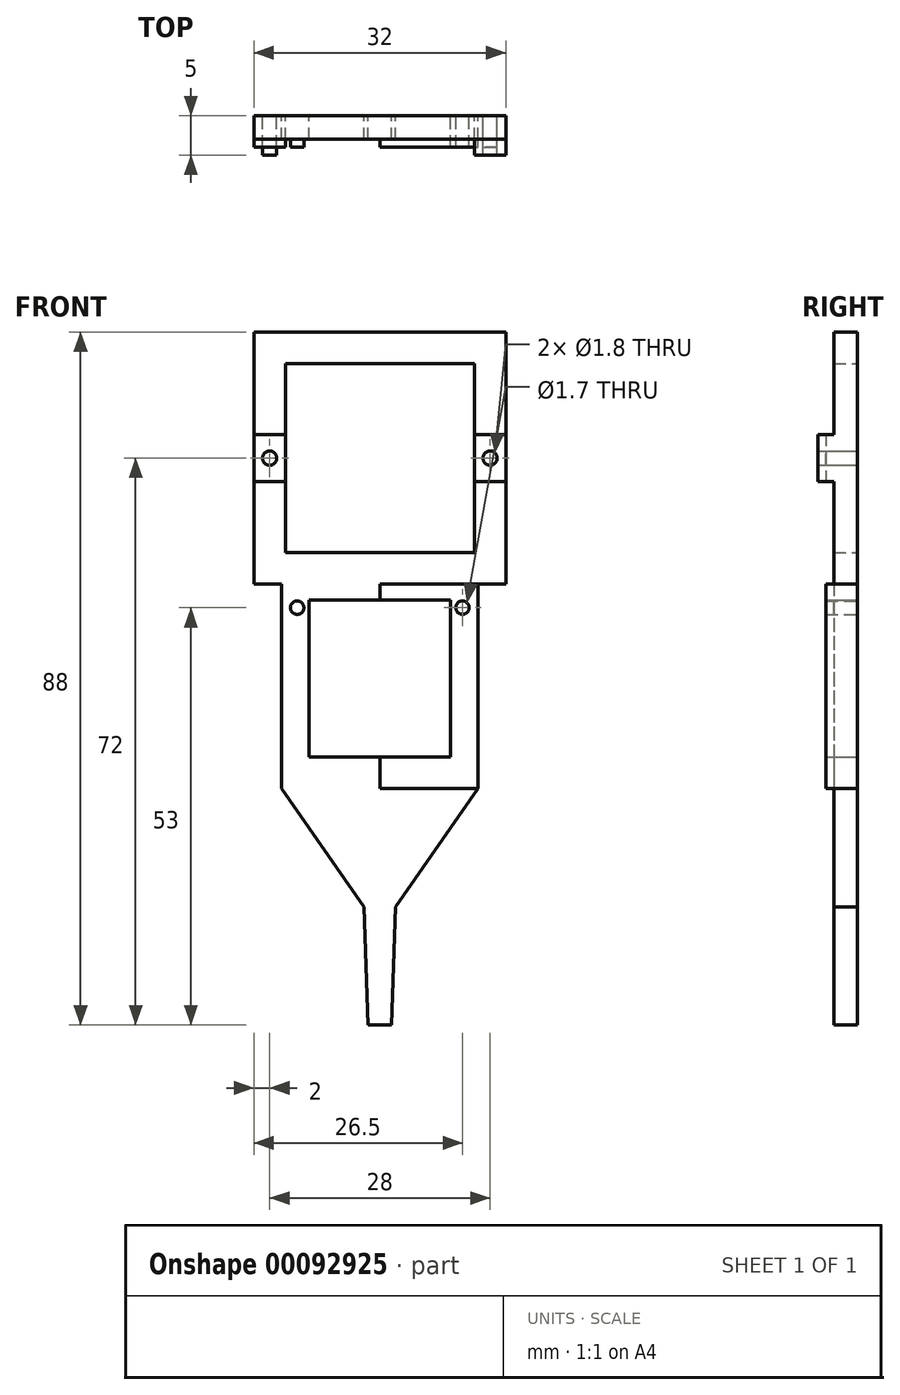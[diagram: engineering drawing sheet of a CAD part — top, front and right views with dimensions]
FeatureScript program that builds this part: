
annotation { "Feature Type Name" : "Feature", "Feature Type Description" : "" }
export const myFeature = defineFeature(function(context is Context, id is Id, definition is map)
    precondition{}
    {
        {
            var Q0;
            Q0=qCreatedBy(makeId("Front.planeOp"),FACE);
            var sketch = newSketch(context, id + "F0", { "sketchPlane" : qUnion([Q0])});
            skLineSegment(sketch, "E0.bottom", {"start": v(-12.5, -4) * mm, "end": v(12.5, -4) * mm});
            skLineSegment(sketch, "E0.top", {"start": v(-12.5, -30) * mm, "end": v(12.5, -30) * mm});
            skLineSegment(sketch, "E0.left", {"start": v(-12.5, -4) * mm, "end": v(-12.5, -30) * mm});
            skLineSegment(sketch, "E0.right", {"start": v(12.5, -4) * mm, "end": v(12.5, -30) * mm});
            skCircle(sketch, "E1", {"center": v(-10.5, -7) * mm, "radius": 0.85 * mm});
            skLineSegment(sketch, "E2", {"start": v(0, 31.04) * mm, "end": v(0, -38.81) * mm});
            skCircle(sketch, "E3.MirrorC", {"center": v(10.5, -7) * mm, "radius": 0.85 * mm});
            skLineSegment(sketch, "E4.bottom", {"start": v(-9, -6) * mm, "end": v(9, -6) * mm});
            skLineSegment(sketch, "E4.top", {"start": v(-9, -26) * mm, "end": v(9, -26) * mm});
            skLineSegment(sketch, "E4.left", {"start": v(-9, -6) * mm, "end": v(-9, -26) * mm});
            skLineSegment(sketch, "E4.right", {"start": v(9, -6) * mm, "end": v(9, -26) * mm});
            skLineSegment(sketch, "E5.MirrorCS", {"start": v(9, -6) * mm, "end": v(-9, -6) * mm});
            skLineSegment(sketch, "E6.MirrorCS", {"start": v(9, -26) * mm, "end": v(-9, -26) * mm});
            skLineSegment(sketch, "E7.bottom", {"start": v(-16, 28) * mm, "end": v(16, 28) * mm});
            skLineSegment(sketch, "E7.top", {"start": v(-16, -4) * mm, "end": v(16, -4) * mm});
            skLineSegment(sketch, "E7.left", {"start": v(-16, 28) * mm, "end": v(-16, -4) * mm});
            skLineSegment(sketch, "E8.bottom", {"start": v(-12, 24) * mm, "end": v(12, 24) * mm});
            skLineSegment(sketch, "E8.top", {"start": v(-12, 0) * mm, "end": v(12, 0) * mm});
            skLineSegment(sketch, "E8.left", {"start": v(-12, 24) * mm, "end": v(-12, 0) * mm});
            skLineSegment(sketch, "E8.right", {"start": v(12, 24) * mm, "end": v(12, 0) * mm});
            skCircle(sketch, "E9", {"center": v(-14, 12) * mm, "radius": 0.9 * mm});
            skLineSegment(sketch, "E10.MirrorCS", {"start": v(0, -39.04) * mm, "end": v(0, 30.81) * mm});
            skCircle(sketch, "E11.MirrorC", {"center": v(14, 12) * mm, "radius": 0.9 * mm});
            skLineSegment(sketch, "E12.bottom", {"start": v(-2, -45) * mm, "end": v(2, -45) * mm});
            skLineSegment(sketch, "E13", {"start": v(-12.5, -30) * mm, "end": v(-2, -45) * mm});
            skLineSegment(sketch, "E14", {"start": v(12.5, -30) * mm, "end": v(2, -45) * mm});
            skLineSegment(sketch, "E15.top", {"start": v(12, 9) * mm, "end": v(16, 9) * mm});
            skLineSegment(sketch, "E15.left", {"start": v(12, 15) * mm, "end": v(12, 9) * mm});
            skLineSegment(sketch, "E15.right", {"start": v(16, 15) * mm, "end": v(16, 9) * mm});
            skLineSegment(sketch, "E16.bottom", {"start": v(-16, 15) * mm, "end": v(-12, 15) * mm});
            skLineSegment(sketch, "E16.top", {"start": v(-16, 9) * mm, "end": v(-12, 9) * mm});
            skLineSegment(sketch, "E16.left", {"start": v(-16, 15) * mm, "end": v(-16, 9) * mm});
            skLineSegment(sketch, "E16.right", {"start": v(-12, 15) * mm, "end": v(-12, 9) * mm});
            skLineSegment(sketch, "E17.bottom", {"start": v(12, 15) * mm, "end": v(16, 15) * mm});
            skLineSegment(sketch, "E18", {"start": v(-2, -45) * mm, "end": v(-1.5, -60) * mm});
            skLineSegment(sketch, "E19", {"start": v(-1.5, -60) * mm, "end": v(1.5, -60) * mm});
            skLineSegment(sketch, "E20", {"start": v(1.5, -60) * mm, "end": v(2, -45) * mm});
            skLineSegment(sketch, "E21", {"start": v(16, -4) * mm, "end": v(16, 28) * mm});
            skSolve(sketch);
        }
        {
            var Q0;
            Q0=makeQuery(id+"F0.imprint","IMPRINT",FACE,{"disambiguationData":[TD([[makeQuery(id+"F0.imprint","IMPRINT",EDGE,{"derivedFrom":sQuery(id+"F0.wireOp",EDGE,"E9")}),1.0]])]});
            var Q1;
            Q1=makeQuery(id+"F0.imprint","IMPRINT",FACE,{"disambiguationData":[TD([[makeQuery(id+"F0.imprint","IMPRINT",EDGE,{"derivedFrom":sQuery(id+"F0.wireOp",EDGE,"E11.MirrorC")}),-1.0]])]});
            extrude(context, id + "F1", {"entities" : qUnion([Q0, Q1]), "depth" : 5 * mm});
        }
        {
            var Q0;
            Q0=makeQuery(id+"F0.imprint","IMPRINT",FACE,{"disambiguationData":[TD([[makeQuery(id+"F0.imprint","IMPRINT",EDGE,{"derivedFrom":sQuery(id+"F0.wireOp",EDGE,"E1")}),1.0]])]});
            var Q1;
            Q1=makeQuery(id+"F0.imprint","IMPRINT",FACE,{"disambiguationData":[TD([[makeQuery(id+"F0.imprint","IMPRINT",EDGE,{"derivedFrom":sQuery(id+"F0.wireOp",EDGE,"42e0c05e-9e20-4baa-a6e4-a09fdd3b6eb8")}),1.0]])]});
            var Q2;
            Q2=makeQuery(id+"F0.imprint","IMPRINT",FACE,{"disambiguationData":[TD([[makeQuery(id+"F0.imprint","IMPRINT",EDGE,{"derivedFrom":sQuery(id+"F0.wireOp",EDGE,"E3.MirrorC")}),-1.0]])]});
            var Q3;
            Q3=makeQuery(id+"F0.imprint","IMPRINT",FACE,{"disambiguationData":[TD([[makeQuery(id+"F0.imprint","IMPRINT",EDGE,{"derivedFrom":sQuery(id+"F0.wireOp",EDGE,"1d1a9675-f9c1-4bd2-a66b-9778542fa53b0.MirrorC")}),-1.0]])]});
            extrude(context, id + "F2", {"entities" : qUnion([Q0, Q1, Q2, Q3]), "depth" : 4 * mm});
        }
        {
            var Q0;
            Q0=makeQuery(id+"F0.imprint","IMPRINT",FACE,{"disambiguationData":[TD([[makeQuery(id+"F0.imprint","IMPRINT",EDGE,{"derivedFrom":sQuery(id+"F0.wireOp",EDGE,"E9")}),-1.0]])]});
            var Q1;
            Q1=makeQuery(id+"F0.imprint","IMPRINT",FACE,{"disambiguationData":[TD([[makeQuery(id+"F0.imprint","IMPRINT",EDGE,{"derivedFrom":sQuery(id+"F0.wireOp",EDGE,"E11.MirrorC")}),1.0]])]});
            extrude(context, id + "F3", {"entities" : qUnion([Q0, Q1]), "depth" : 4 * mm});
        }
        {
            var Q0;
            {var subQ8=sQuery(id+"F0.wireOp",EDGE,"E16.bottom");Q0=makeQuery(id+"F0.imprint","IMPRINT",FACE,{"disambiguationData":[TD([[makeQuery(id+"F0.imprint","IMPRINT",EDGE,{"derivedFrom":subQ8}),1.0]])]});}
            var Q1;
            {var subQ9=sQuery(id+"F0.wireOp",EDGE,"E17.bottom");Q1=makeQuery(id+"F0.imprint","IMPRINT",FACE,{"disambiguationData":[TD([[makeQuery(id+"F0.imprint","IMPRINT",EDGE,{"derivedFrom":subQ9}),1.0]])]});}
            var Q2;
            {var subQ12=sQuery(id+"F0.wireOp",EDGE,"E15.top");Q2=makeQuery(id+"F0.imprint","IMPRINT",FACE,{"disambiguationData":[TD([[makeQuery(id+"F0.imprint","IMPRINT",EDGE,{"derivedFrom":subQ12}),-1.0]])]});}
            var Q3;
            {var subQ8=sQuery(id+"F0.wireOp",EDGE,"E16.top");Q3=makeQuery(id+"F0.imprint","IMPRINT",FACE,{"disambiguationData":[TD([[makeQuery(id+"F0.imprint","IMPRINT",EDGE,{"derivedFrom":subQ8}),-1.0]])]});}
            var Q4;
            {var subQ5=sQuery(id+"F0.wireOp",EDGE,"E0.left");Q4=makeQuery(id+"F0.imprint","IMPRINT",FACE,{"disambiguationData":[TD([[makeQuery(id+"F0.imprint","IMPRINT",EDGE,{"derivedFrom":subQ5}),1.0]])]});}
            var Q5;
            {var subQ1=sQuery(id+"F0.wireOp",EDGE,"E0.right");Q5=makeQuery(id+"F0.imprint","IMPRINT",FACE,{"disambiguationData":[TD([[makeQuery(id+"F0.imprint","IMPRINT",EDGE,{"derivedFrom":subQ1}),-1.0]])]});}
            extrude(context, id + "F4", {"entities" : qUnion([Q0, Q1, Q2, Q3, Q4, Q5]), "operationType" : NewBodyOperationType.ADD, "depth" : 3 * mm});
        }
        {
            var Q0;
            Q0=makeQuery(id+"F0.imprint","IMPRINT",FACE,{"disambiguationData":[TD([[makeQuery(id+"F0.imprint","IMPRINT",EDGE,{"derivedFrom":sQuery(id+"F0.wireOp",EDGE,"E12.bottom")}),1.0]])]});
            var Q1;
            Q1=makeQuery(id+"F0.imprint","IMPRINT",FACE,{"disambiguationData":[TD([[makeQuery(id+"F0.imprint","IMPRINT",EDGE,{"derivedFrom":sQuery(id+"F0.wireOp",EDGE,"E12.bottom")}),-1.0]])]});
            extrude(context, id + "F5", {"entities" : qUnion([Q0, Q1]), "operationType" : NewBodyOperationType.ADD, "depth" : 3 * mm});
        }
    });
